# Revit family: Specialty_Equipment-Planter-Planters_Unlimited-Modern-Rocca Tapered square-rev
name_source: partatom
category: Specialty Equipment
units: mm (PartAtom-declared; Revit-internal decimal feet)

## family parameters
Always vertical = Yes
Cut with Voids When Loaded = No
Enable Cutting in Views = No
Maintain Annotation Orientation = No
OmniClass Number = 23.40.05.21.17
OmniClass Title = Planters
Part Type = Normal
Room Calculation Point = No
Round Connector Dimension = Use Diameter
Shared = No
Work Plane-Based = No

## types (1)
- default load type catalog
    Assembly Code = G2050600
    CD_Diameter Bottom = 305 mm  [stored 1.00066 ft]
    CD_Diameter Top = 610 mm  [stored 2.00131 ft]
    CD_Finish = Fiberglass
    CD_Height = 610 mm  [stored 2.00131 ft]
    CD_Offset = 3 mm  [stored 0.00984252 ft]
    CD_Product Page URL = https://www.plantersunlimited.com
    CD_Specification = https://www.plantersunlimited.com
    Default Elevation = 0 mm  [stored 0 ft]
    Description = Modular Planting Bed
    Manufacturer = Planters Unlimited
    Model = Modern Series Planters
    Type Comments = Rocca Fiberglass Tapered Square Planter
    URL = https://www.plantersunlimited.com

note: [stored X ft] marks values corroborated as IEEE doubles in the binary element streams (Revit-internal decimal feet)

## geometry (parser evidence)
native form markers: Sweep x3
no freeform markers — native parametric forms only
